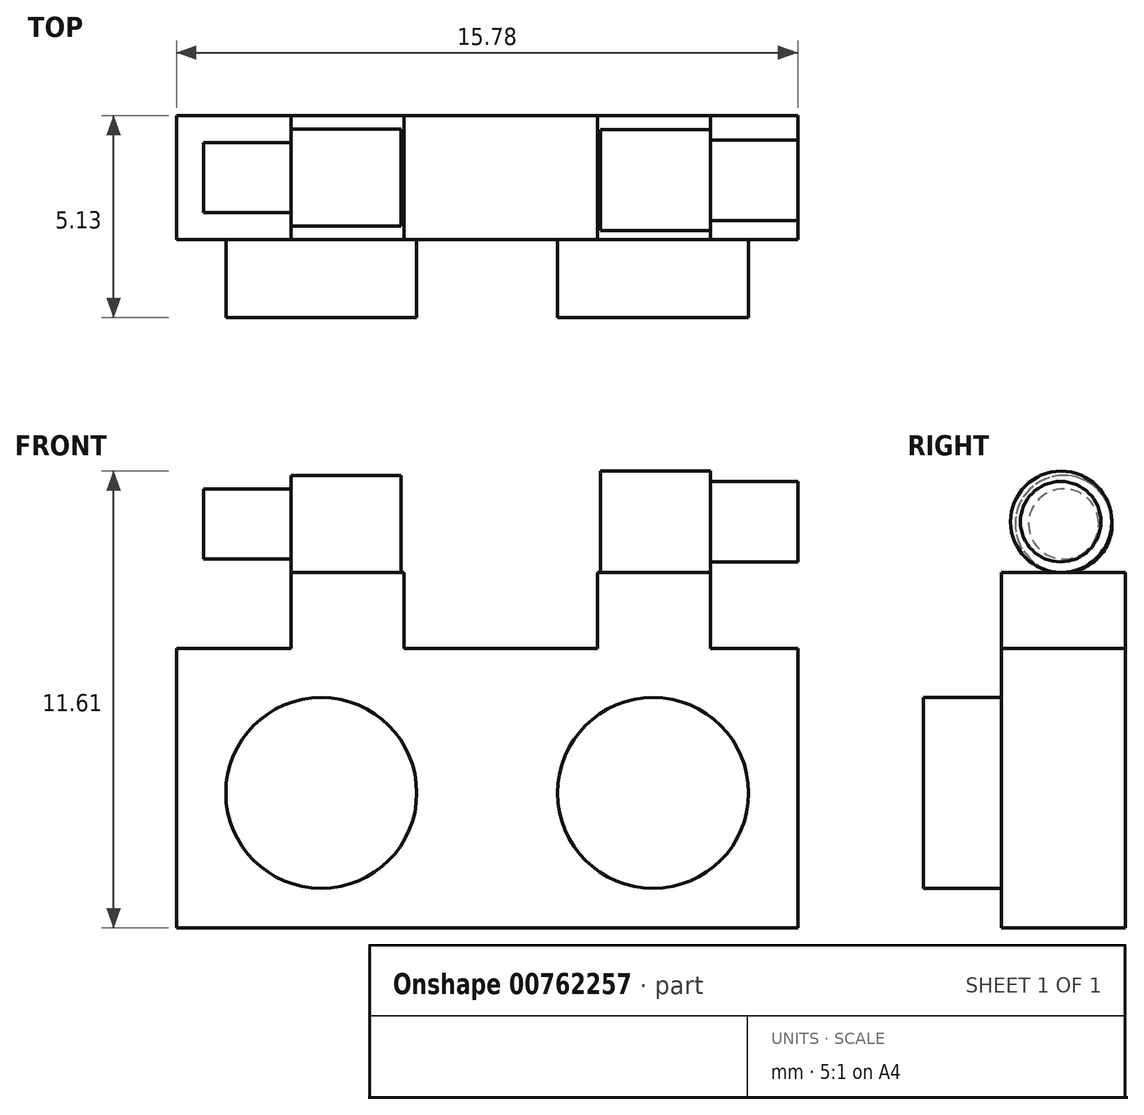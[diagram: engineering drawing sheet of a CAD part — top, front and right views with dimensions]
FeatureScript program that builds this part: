
annotation { "Feature Type Name" : "Feature", "Feature Type Description" : "" }
export const myFeature = defineFeature(function(context is Context, id is Id, definition is map)
    precondition{}
    {
        {
            var Q0;
            Q0=qCreatedBy(makeId("Front.planeOp"),FACE);
            var sketch = newSketch(context, id + "F0", { "sketchPlane" : qUnion([Q0])});
            skLineSegment(sketch, "E0.bottom", {"start": v(-66.46, 18.15) * mm, "end": v(-50.68, 18.15) * mm});
            skLineSegment(sketch, "E0.top", {"start": v(-66.46, 11.05) * mm, "end": v(-50.68, 11.05) * mm});
            skLineSegment(sketch, "E0.left", {"start": v(-50.68, 18.15) * mm, "end": v(-50.68, 11.05) * mm});
            skLineSegment(sketch, "E0.right", {"start": v(-66.46, 18.15) * mm, "end": v(-66.46, 11.05) * mm});
            skLineSegment(sketch, "E1", {"start": v(-64.02, 22.58) * mm, "end": v(-62.73, 22.58) * mm});
            skPoint(sketch, "E2.startSnap0", {"position": v(-62.73, 20.36) * mm});
            skSolve(sketch);
        }
        {
            var Q0;
            Q0=qSketchRegion(id+"F0",true);
            extrude(context, id + "F1", {"entities" : qUnion([Q0]), "depth" : 3.15 * mm, "offsetDistance" : 25 * mm});
        }
        {
            var Q0;
            Q0=makeQuery(id+"F1.opExtrude","CAP_FACE",FACE,{"disambiguationData":[OSD([sQuery(id+"F0.wireOp",EDGE,"E0.bottom"),sQuery(id+"F0.wireOp",EDGE,"E0.top"),sQuery(id+"F0.wireOp",EDGE,"E0.left"),sQuery(id+"F0.wireOp",EDGE,"E0.right")])],"isStart":false});
            var sketch = newSketch(context, id + "F2", { "sketchPlane" : qUnion([Q0])});
            skCircle(sketch, "E3", {"center": v(-62.78, 14.48) * mm, "radius": 2.43 * mm});
            skCircle(sketch, "E4", {"center": v(-54.35, 14.48) * mm, "radius": 2.43 * mm});
            skPoint(sketch, "E5.start.orphan", {"position": v(-62.78, 16.9) * mm});
            skPoint(sketch, "E6.start.orphan", {"position": v(-54.35, 16.9) * mm});
            skPoint(sketch, "E7.start.orphan", {"position": v(-51.93, 14.48) * mm});
            skPoint(sketch, "E8.start.orphan", {"position": v(-65.2, 14.48) * mm});
            skSolve(sketch);
        }
        {
            var Q0;
            Q0=qSketchRegion(id+"F2",true);
            extrude(context, id + "F3", {"entities" : qUnion([Q0]), "operationType" : NewBodyOperationType.ADD, "depth" : 1.98 * mm, "offsetDistance" : 25 * mm});
        }
        {
            var Q0;
            Q0=makeQuery(id+"F1.opExtrude","SWEPT_FACE",FACE,{"disambiguationData":[OSD([sQuery(id+"F0.wireOp",EDGE,"E0.bottom")])]});
            var sketch = newSketch(context, id + "F4", { "sketchPlane" : qUnion([Q0])});
            skLineSegment(sketch, "E9.bottom", {"start": v(-63.55, -3.15) * mm, "end": v(-60.68, -3.15) * mm});
            skLineSegment(sketch, "E9.top", {"start": v(-63.55, 0) * mm, "end": v(-60.68, 0) * mm});
            skLineSegment(sketch, "E9.left", {"start": v(-63.55, -3.15) * mm, "end": v(-63.55, 0) * mm});
            skLineSegment(sketch, "E9.right", {"start": v(-60.68, -3.15) * mm, "end": v(-60.68, 0) * mm});
            skLineSegment(sketch, "E10.bottom", {"start": v(-55.77, -3.15) * mm, "end": v(-52.9, -3.15) * mm});
            skLineSegment(sketch, "E10.top", {"start": v(-55.77, 0) * mm, "end": v(-52.9, 0) * mm});
            skLineSegment(sketch, "E10.left", {"start": v(-55.77, -3.15) * mm, "end": v(-55.77, 0) * mm});
            skLineSegment(sketch, "E10.right", {"start": v(-52.9, -3.15) * mm, "end": v(-52.9, 0) * mm});
            skSolve(sketch);
        }
        {
            var Q0;
            Q0 = qSketchRegion(id + "F4", true);
            extrude(context, id + "F5", {"entities" : qUnion([Q0]), "operationType" : NewBodyOperationType.ADD, "depth" : 1.93 * mm, "offsetDistance" : 25 * mm});
        }
        {
            var Q0;
            Q0=makeQuery(id+"F5.opExtrude","SWEPT_FACE",FACE,{"disambiguationData":[OSD([sQuery(id+"F4.wireOp",EDGE,"E10.right")])]});
            var sketch = newSketch(context, id + "F6", { "sketchPlane" : qUnion([Q0])});
            skCircle(sketch, "E11", {"center": v(-1.64, 21.37) * mm, "radius": 1.29 * mm});
            skPoint(sketch, "E11.centerSnap0", {"position": v(-3.15, 21.37) * mm});
            skPoint(sketch, "E12.orphan", {"position": v(-3.15, 22.66) * mm});
            skPoint(sketch, "E13.right.end.orphan", {"position": v(0, 22.66) * mm});
            skPoint(sketch, "E13.bottom.start.orphan", {"position": v(-3.15, 20.08) * mm});
            skSolve(sketch);
        }
        {
            var Q0;
            Q0 = qSketchRegion(id + "F6", true);
            extrude(context, id + "F7", {"entities" : qUnion([Q0]), "oppositeDirection" : true, "depth" : 2.8 * mm, "offsetDistance" : 25 * mm});
        }
        {
            var Q0;
            Q0=makeQuery(id+"F7.opExtrude","CAP_FACE",FACE,{"disambiguationData":[OSD([sQuery(id+"F6.wireOp",EDGE,"E11")])],"isStart":true});
            var sketch = newSketch(context, id + "F8", { "sketchPlane" : qUnion([Q0])});
            skCircle(sketch, "E14", {"center": v(-1.64, 21.37) * mm, "radius": 0.86 * mm});
            skSolve(sketch);
        }
        {
            var Q0;
            Q0=makeQuery(id+"F5.opExtrude","SWEPT_FACE",FACE,{"disambiguationData":[OSD([sQuery(id+"F4.wireOp",EDGE,"E9.left")])]});
            var sketch = newSketch(context, id + "F9", { "sketchPlane" : qUnion([Q0])});
            skLineSegment(sketch, "E15", {"start": v(1.57, 20.08) * mm, "end": v(1.57, 21.32) * mm});
            skCircle(sketch, "E16", {"center": v(1.57, 21.32) * mm, "radius": 1.23 * mm});
            skSolve(sketch);
        }
        {
            var Q0;
            Q0 = qSketchRegion(id + "F9", true);
            extrude(context, id + "F10", {"entities" : qUnion([Q0]), "oppositeDirection" : true, "depth" : 2.8 * mm, "offsetDistance" : 25 * mm});
        }
        {
            var Q0;
            Q0=makeQuery(id+"F8.imprint","IMPRINT",FACE,{"disambiguationData":[TD([[makeQuery(id+"F8.imprint","IMPRINT",EDGE,{"derivedFrom":sQuery(id+"F8.wireOp",EDGE,"E14")}),1.0]])]});
            var sketch = newSketch(context, id + "F11", { "sketchPlane" : qUnion([Q0])});
            skCircle(sketch, "E17", {"center": v(-1.65, 21.37) * mm, "radius": 1.02 * mm});
            skSolve(sketch);
        }
        {
            var Q0;
            Q0 = qSketchRegion(id + "F11", true);
            extrude(context, id + "F12", {"entities" : qUnion([Q0]), "operationType" : NewBodyOperationType.ADD, "depth" : 2.22 * mm, "offsetDistance" : 25 * mm});
        }
        {
            var Q0;
            Q0=makeQuery(id+"F10.opExtrude","CAP_FACE",FACE,{"disambiguationData":[OSD([sQuery(id+"F9.wireOp",EDGE,"E16")])],"isStart":true});
            var sketch = newSketch(context, id + "F13", { "sketchPlane" : qUnion([Q0])});
            skCircle(sketch, "E18", {"center": v(1.57, 21.32) * mm, "radius": 0.9 * mm});
            skSolve(sketch);
        }
        {
            var Q0;
            Q0=makeQuery(id+"F13.imprint","IMPRINT",FACE,{"disambiguationData":[TD([[makeQuery(id+"F13.imprint","IMPRINT",EDGE,{"derivedFrom":sQuery(id+"F13.wireOp",EDGE,"E18")}),1.0]])]});
            extrude(context, id + "F14", {"entities" : qUnion([Q0]), "operationType" : NewBodyOperationType.ADD, "depth" : 2.22 * mm, "offsetDistance" : 25 * mm});
        }
    });
